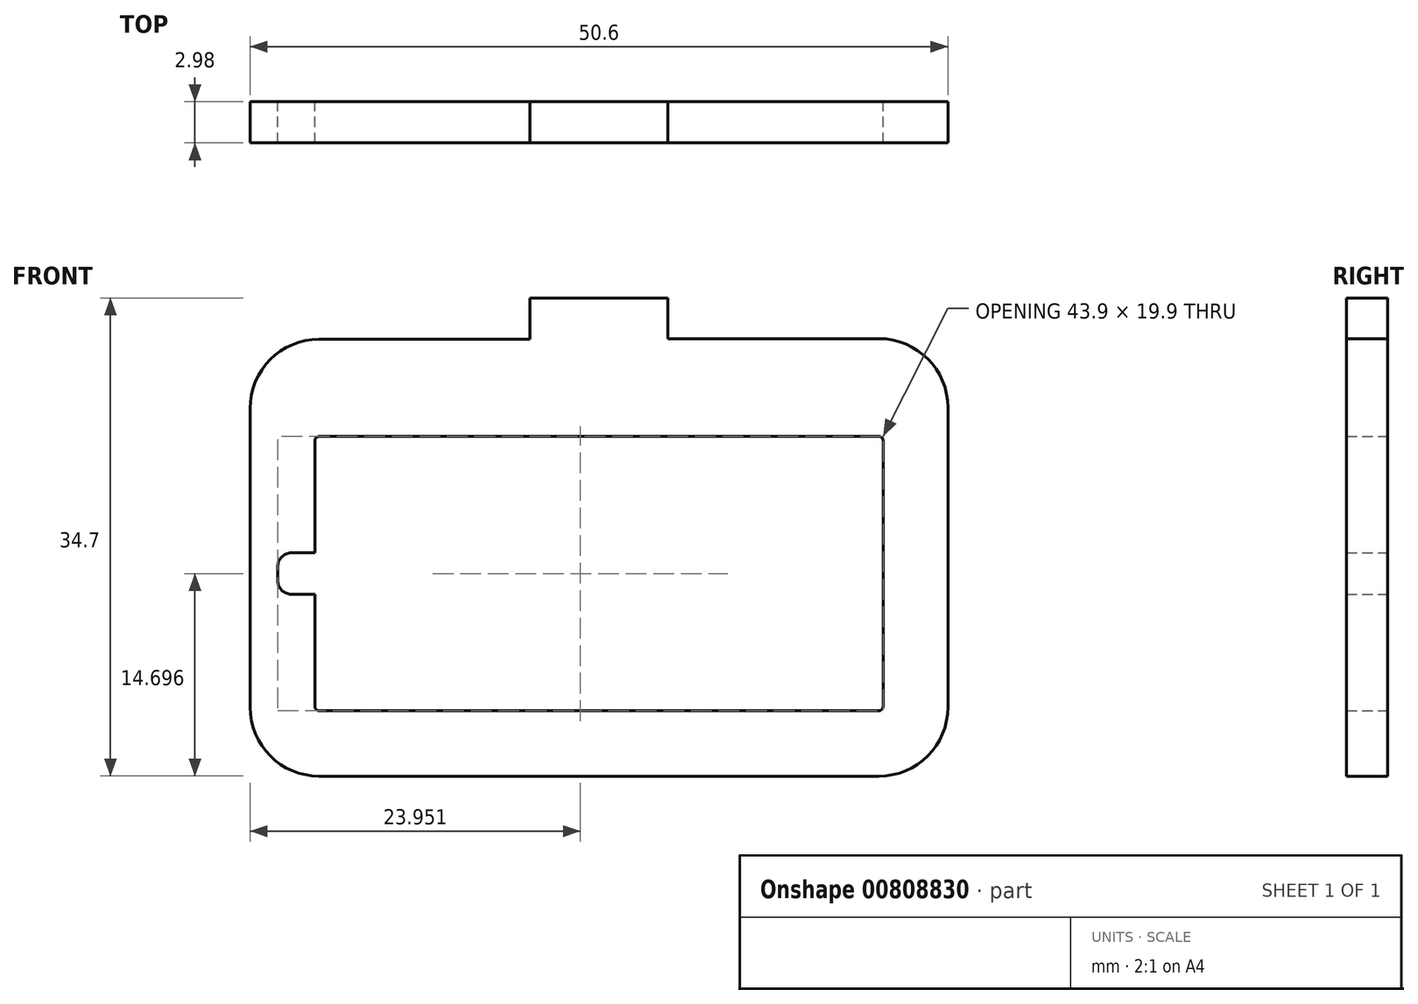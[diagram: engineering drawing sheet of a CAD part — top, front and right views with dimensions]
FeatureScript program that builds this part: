
annotation { "Feature Type Name" : "Feature", "Feature Type Description" : "" }
export const myFeature = defineFeature(function(context is Context, id is Id, definition is map)
    precondition{}
    {
        {
            var Q0;
            Q0=qCreatedBy(makeId("Front.planeOp"),FACE);
            var sketch = newSketch(context, id + "F0", { "sketchPlane" : qUnion([Q0])});
            skLineSegment(sketch, "E0.2", {"start": v(25.42, -65.46) * mm, "end": v(-49.58, -65.46) * mm});
            skPoint(sketch, "E0.0.midPoint", {"position": v(-39.22, 12.48) * mm});
            skPoint(sketch, "E1.visualSharp", {"position": v(-84.22, -65.46) * mm});
            skArc(sketch, "E1.filletArc", {"start": v(-64.59, -32.24) * mm, "mid": v(-67.8, -53.7) * mm, "end": v(-49.58, -65.46) * mm});
            skLineSegment(sketch, "E2.bottom", {"start": v(55.42, -5.46) * mm, "end": v(19.77, -5.46) * mm});
            skLineSegment(sketch, "E2.top", {"start": v(55.42, 94.54) * mm, "end": v(-44.58, 94.54) * mm});
            skLineSegment(sketch, "E2.left", {"start": v(55.42, -5.46) * mm, "end": v(55.42, 94.54) * mm});
            skLineSegment(sketch, "E2.right", {"start": v(-44.58, -5.46) * mm, "end": v(-44.58, 94.54) * mm});
            skPoint(sketch, "E2.middle", {"position": v(5.42, 44.54) * mm});
            skPoint(sketch, "E3.visualSharp", {"position": v(105.78, -65.46) * mm});
            skArc(sketch, "E3.filletArc", {"start": v(25.42, -65.46) * mm, "mid": v(62.94, -39.32) * mm, "end": v(51.42, 4.93) * mm});
            skPoint(sketch, "E4.visualSharp", {"position": v(5.78, 90.42) * mm});
            skCircle(sketch, "E5", {"center": v(-49.58, -45.46) * mm, "radius": 1.5 * mm});
            skCircle(sketch, "E6", {"center": v(25.42, -25.46) * mm, "radius": 1.5 * mm});
            skArc(sketch, "E7", {"start": v(15.17, 35.94) * mm, "mid": v(4.36, 39.5) * mm, "end": v(-5.83, 34.45) * mm});
            skCircle(sketch, "E8", {"center": v(5.42, 24.54) * mm, "radius": 1.5 * mm});
            skLineSegment(sketch, "E9", {"start": v(15.17, 35.94) * mm, "end": v(51.42, 4.93) * mm});
            skPoint(sketch, "E10.orphan", {"position": v(5.11, 44.54) * mm});
            skLineSegment(sketch, "E11", {"start": v(-64.59, -32.24) * mm, "end": v(-5.83, 34.45) * mm});
            skArc(sketch, "E12.0", {"start": v(-57.08, -38.85) * mm, "mid": v(-58.7, -49.58) * mm, "end": v(-49.58, -55.46) * mm});
            skArc(sketch, "E12.1", {"start": v(8.67, 28.34) * mm, "mid": v(5.07, 29.52) * mm, "end": v(1.67, 27.84) * mm});
            skLineSegment(sketch, "E12.2", {"start": v(8.67, 28.34) * mm, "end": v(44.92, -2.67) * mm});
            skLineSegment(sketch, "E12.3", {"start": v(-57.08, -38.85) * mm, "end": v(1.67, 27.84) * mm});
            skArc(sketch, "E12.4", {"start": v(25.42, -55.46) * mm, "mid": v(53.56, -35.86) * mm, "end": v(44.92, -2.67) * mm});
            skLineSegment(sketch, "E12.5", {"start": v(25.42, -55.46) * mm, "end": v(-49.58, -55.46) * mm});
            skLineSegment(sketch, "E13.bottom", {"start": v(15.42, -1.91) * mm, "end": v(25.42, -1.91) * mm});
            skLineSegment(sketch, "E13.top", {"start": v(15.42, 0.99) * mm, "end": v(25.42, 0.99) * mm});
            skLineSegment(sketch, "E13.left", {"start": v(15.42, -1.91) * mm, "end": v(15.42, 0.99) * mm});
            skLineSegment(sketch, "E13.right", {"start": v(25.42, -1.91) * mm, "end": v(25.42, 0.99) * mm});
            skPoint(sketch, "E13.middle", {"position": v(20.42, -0.46) * mm});
            skLineSegment(sketch, "E14.bottom", {"start": v(-14.58, -1.95) * mm, "end": v(-4.58, -1.95) * mm});
            skLineSegment(sketch, "E14.top", {"start": v(-14.58, 1.03) * mm, "end": v(-4.58, 1.03) * mm});
            skLineSegment(sketch, "E14.left", {"start": v(-14.58, -1.95) * mm, "end": v(-14.58, 1.03) * mm});
            skLineSegment(sketch, "E14.right", {"start": v(-4.58, -1.95) * mm, "end": v(-4.58, 1.03) * mm});
            skPoint(sketch, "E14.middle", {"position": v(-9.58, -0.46) * mm});
            skLineSegment(sketch, "E15.bottom", {"start": v(10.42, 11.03) * mm, "end": v(0.42, 11.03) * mm});
            skLineSegment(sketch, "E15.top", {"start": v(10.42, 8.05) * mm, "end": v(0.42, 8.05) * mm});
            skLineSegment(sketch, "E15.left", {"start": v(10.42, 11.03) * mm, "end": v(10.42, 8.05) * mm});
            skLineSegment(sketch, "E15.right", {"start": v(0.42, 11.03) * mm, "end": v(0.42, 8.05) * mm});
            skPoint(sketch, "E15.middle", {"position": v(5.42, 9.54) * mm});
            skCircle(sketch, "E16", {"center": v(-46.08, -40.46) * mm, "radius": 1.5 * mm});
            skCircle(sketch, "E17", {"center": v(25.42, -25.46) * mm, "radius": 6.25 * mm});
            skLineSegment(sketch, "E18.bottom", {"start": v(-5.53, -15.81) * mm, "end": v(35.07, -15.81) * mm});
            skLineSegment(sketch, "E18.top", {"start": v(-5.53, -35.11) * mm, "end": v(35.07, -35.11) * mm});
            skLineSegment(sketch, "E18.left", {"start": v(-5.53, -15.81) * mm, "end": v(-5.53, -35.11) * mm});
            skLineSegment(sketch, "E18.right", {"start": v(35.07, -15.81) * mm, "end": v(35.07, -35.11) * mm});
            skLineSegment(sketch, "E19.1", {"start": v(-10.53, -15.86) * mm, "end": v(-10.53, -35.16) * mm});
            skLineSegment(sketch, "E19.2", {"start": v(-5.53, -40.16) * mm, "end": v(35.07, -40.16) * mm});
            skLineSegment(sketch, "E19.3", {"start": v(40.07, -13.41) * mm, "end": v(40.07, -35.16) * mm});
            skLineSegment(sketch, "E20.bottom", {"start": v(-2.53, -26.96) * mm, "end": v(-7.53, -26.96) * mm});
            skLineSegment(sketch, "E20.top", {"start": v(-2.53, -23.96) * mm, "end": v(-7.53, -23.96) * mm});
            skLineSegment(sketch, "E20.left", {"start": v(-2.53, -26.96) * mm, "end": v(-2.53, -23.96) * mm});
            skLineSegment(sketch, "E20.right", {"start": v(-8.53, -25.96) * mm, "end": v(-8.53, -24.96) * mm});
            skPoint(sketch, "E20.middle", {"position": v(-5.53, -25.46) * mm});
            skPoint(sketch, "E21.middle", {"position": v(14.77, -10.81) * mm});
            skPoint(sketch, "E22.visualSharp", {"position": v(40.07, -10.81) * mm});
            skPoint(sketch, "E23.visualSharp", {"position": v(40.07, -40.16) * mm});
            skArc(sketch, "E23.filletArc", {"start": v(35.07, -40.16) * mm, "mid": v(38.6, -38.7) * mm, "end": v(40.07, -35.16) * mm});
            skPoint(sketch, "E24.visualSharp", {"position": v(-10.53, -40.16) * mm});
            skArc(sketch, "E24.filletArc", {"start": v(-10.53, -35.16) * mm, "mid": v(-9.06, -38.7) * mm, "end": v(-5.53, -40.16) * mm});
            skPoint(sketch, "E25.visualSharp", {"position": v(-10.53, -10.81) * mm});
            skLineSegment(sketch, "E26.trimOffspring", {"start": v(19.77, -15.81) * mm, "end": v(19.77, -16.16) * mm});
            skPoint(sketch, "E27.visualSharp", {"position": v(19.77, -10.81) * mm});
            skPoint(sketch, "E28.visualSharp", {"position": v(9.77, -10.86) * mm});
            skPoint(sketch, "E29.visualSharp", {"position": v(-8.53, -23.96) * mm});
            skArc(sketch, "E29.filletArc", {"start": v(-7.53, -23.96) * mm, "mid": v(-8.24, -24.26) * mm, "end": v(-8.53, -24.96) * mm});
            skPoint(sketch, "E30.visualSharp", {"position": v(-8.53, -26.96) * mm});
            skArc(sketch, "E30.filletArc", {"start": v(-8.53, -25.96) * mm, "mid": v(-8.24, -26.67) * mm, "end": v(-7.53, -26.96) * mm});
            skLineSegment(sketch, "E31.trimOffspring", {"start": v(9.77, -5.46) * mm, "end": v(-44.58, -5.46) * mm});
            skPoint(sketch, "E32.right.start.orphan", {"position": v(9.77, -5.46) * mm});
            skPoint(sketch, "E21.bottom.start.orphan", {"position": v(14.77, -5.46) * mm});
            skLineSegment(sketch, "E33.left", {"start": v(9.77, -10.86) * mm, "end": v(9.77, -8.46) * mm});
            skLineSegment(sketch, "E33.right", {"start": v(19.77, -10.86) * mm, "end": v(19.77, -8.41) * mm});
            skLineSegment(sketch, "E34.top", {"start": v(9.77, -5.46) * mm, "end": v(19.77, -5.46) * mm});
            skLineSegment(sketch, "E34.left", {"start": v(9.77, -8.46) * mm, "end": v(9.77, -5.46) * mm});
            skLineSegment(sketch, "E34.right", {"start": v(19.77, -8.46) * mm, "end": v(19.77, -5.46) * mm});
            skLineSegment(sketch, "E35", {"start": v(-10.53, -15.86) * mm, "end": v(-10.53, -13.46) * mm});
            skLineSegment(sketch, "E36", {"start": v(-5.53, -8.46) * mm, "end": v(9.77, -8.46) * mm});
            skLineSegment(sketch, "E37", {"start": v(19.77, -8.41) * mm, "end": v(35.07, -8.41) * mm});
            skPoint(sketch, "E38.orphan", {"position": v(40.07, -15.81) * mm});
            skPoint(sketch, "E39.visualSharp", {"position": v(-10.53, -8.46) * mm});
            skArc(sketch, "E39.filletArc", {"start": v(-5.53, -8.46) * mm, "mid": v(-9.06, -9.93) * mm, "end": v(-10.53, -13.46) * mm});
            skPoint(sketch, "E40.visualSharp", {"position": v(40.07, -8.41) * mm});
            skArc(sketch, "E40.filletArc", {"start": v(40.07, -13.41) * mm, "mid": v(38.6, -9.88) * mm, "end": v(35.07, -8.41) * mm});
            skLineSegment(sketch, "E41.bottom", {"start": v(19, -47.45) * mm, "end": v(10.54, -47.45) * mm});
            skLineSegment(sketch, "E41.top", {"start": v(19, -32.88) * mm, "end": v(10.54, -32.88) * mm});
            skLineSegment(sketch, "E41.left", {"start": v(19, -47.45) * mm, "end": v(19, -32.88) * mm});
            skLineSegment(sketch, "E41.right", {"start": v(10.54, -47.45) * mm, "end": v(10.54, -32.88) * mm});
            skPoint(sketch, "E41.middle", {"position": v(14.77, -40.16) * mm});
            skLineSegment(sketch, "E42.0", {"start": v(-5.53, -15.51) * mm, "end": v(35.07, -15.51) * mm});
            skLineSegment(sketch, "E42.1", {"start": v(-5.83, -15.81) * mm, "end": v(-5.83, -35.11) * mm});
            skLineSegment(sketch, "E42.2", {"start": v(-5.53, -35.41) * mm, "end": v(35.07, -35.41) * mm});
            skLineSegment(sketch, "E42.3", {"start": v(35.37, -15.81) * mm, "end": v(35.37, -35.11) * mm});
            skPoint(sketch, "E43.visualSharp", {"position": v(-5.83, -35.41) * mm});
            skArc(sketch, "E43.filletArc", {"start": v(-5.83, -35.11) * mm, "mid": v(-5.74, -35.33) * mm, "end": v(-5.53, -35.41) * mm});
            skPoint(sketch, "E44.visualSharp", {"position": v(35.37, -35.41) * mm});
            skArc(sketch, "E44.filletArc", {"start": v(35.07, -35.41) * mm, "mid": v(35.28, -35.33) * mm, "end": v(35.37, -35.11) * mm});
            skPoint(sketch, "E45.visualSharp", {"position": v(35.37, -15.51) * mm});
            skArc(sketch, "E45.filletArc", {"start": v(35.37, -15.81) * mm, "mid": v(35.28, -15.6) * mm, "end": v(35.07, -15.51) * mm});
            skPoint(sketch, "E46.visualSharp", {"position": v(-5.83, -15.51) * mm});
            skArc(sketch, "E46.filletArc", {"start": v(-5.53, -15.51) * mm, "mid": v(-5.74, -15.6) * mm, "end": v(-5.83, -15.81) * mm});
            skSolve(sketch);
        }
        {
            var Q0;
            {var subQ0=sQuery(id+"F0.wireOp",EDGE,"E41.right");var subQ1=sQuery(id+"F0.wireOp",EDGE,"E19.2");var subQ2=makeQuery(id+"F0.imprint","INTERSECT",VERTEX,{"derivedFrom":[subQ1,subQ0]});Q0=makeQuery(id+"F0.imprint","IMPRINT",FACE,{"disambiguationData":[TD([[makeQuery(id+"F0.imprint","IMPRINT",EDGE,{"disambiguationData":[TD([[subQ2,-1.0]])],"derivedFrom":subQ1}),1.0]])]});}
            var Q1;
            Q1=makeQuery(id+"F0.imprint","IMPRINT",FACE,{"disambiguationData":[TD([[makeQuery(id+"F0.imprint","IMPRINT",EDGE,{"derivedFrom":sQuery(id+"F0.wireOp",EDGE,"E19.1")}),1.0]])]});
            extrude(context, id + "F1", {"entities" : qUnion([Q0, Q1]), "depth" : 2.98 * mm, "offsetDistance" : 25 * mm});
        }
    });
